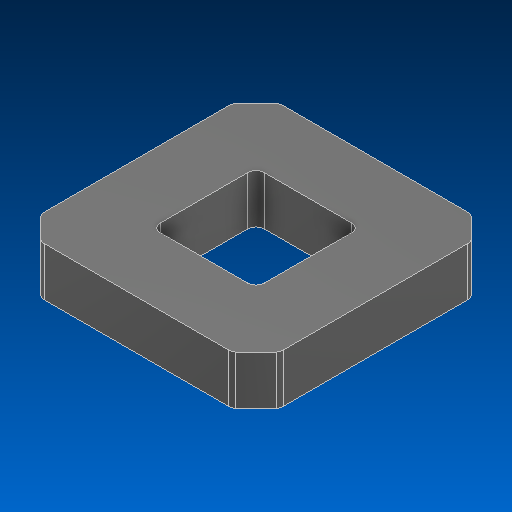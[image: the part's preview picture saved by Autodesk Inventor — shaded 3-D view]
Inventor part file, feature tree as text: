
AUTODESK INVENTOR PART (.ipt)
format: ipt  version: 2022.2 (Build 262287000, 287)  size: 108,032 bytes
history: native  units: in
note: dims shown in document units (in); Inventor stores cm internally (conversion verified against a paired STEP export)
features: fillet x1
ambient origin geometry x8: Origin, YZ Plane, XZ Plane, XY Plane, X Axis, Y Axis, Z Axis, Center Point
bodies: Solid1 (feature_tree)
feature tree (1):
  fillet  "Fillet1"  [1 undecoded]
note: 1 required parameter value undecoded (feature->parameter linkage not recoverable at this tier; creation-order binding heuristic only, values carry confidence <= 0.55)
